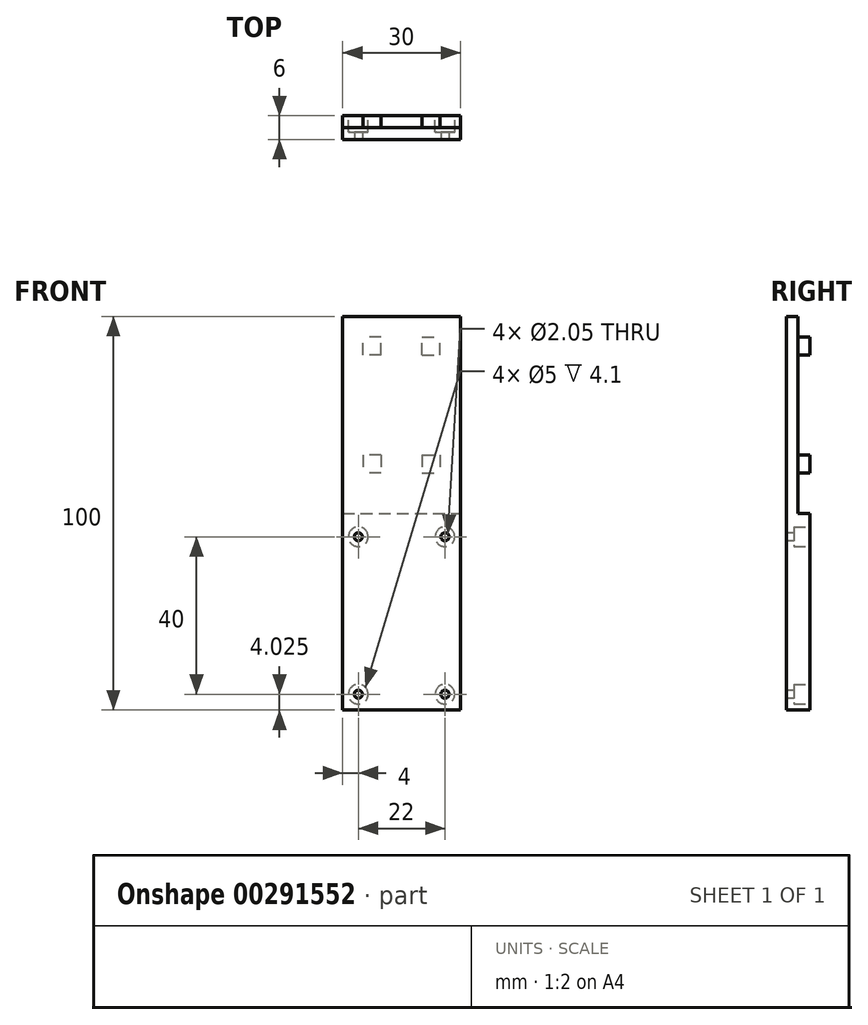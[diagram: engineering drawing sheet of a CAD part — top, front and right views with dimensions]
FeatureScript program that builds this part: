
annotation { "Feature Type Name" : "Feature", "Feature Type Description" : "" }
export const myFeature = defineFeature(function(context is Context, id is Id, definition is map)
    precondition{}
    {
        {
            var Q0;
            Q0=qCreatedBy(makeId("Top.planeOp"),FACE);
            var sketch = newSketch(context, id + "F0", { "sketchPlane" : qUnion([Q0])});
            skLineSegment(sketch, "E0.bottom", {"start": v(-15, 3) * mm, "end": v(15, 3) * mm});
            skLineSegment(sketch, "E0.top", {"start": v(-15, -3) * mm, "end": v(15, -3) * mm});
            skLineSegment(sketch, "E0.left", {"start": v(-15, 3) * mm, "end": v(-15, -3) * mm});
            skLineSegment(sketch, "E0.right", {"start": v(15, 3) * mm, "end": v(15, -3) * mm});
            skSolve(sketch);
        }
        {
            var Q0;
            Q0=qSketchRegion(id+"F0",true);
            extrude(context, id + "F1", {"entities" : qUnion([Q0]), "depth" : 100 * mm, "offsetDistance" : 25 * mm});
        }
        {
            var Q0;
            Q0=makeQuery(id+"F1.opExtrude","SWEPT_FACE",FACE,{"disambiguationData":[OSD([sQuery(id+"F0.wireOp",EDGE,"E0.top")])]});
            var sketch = newSketch(context, id + "F2", { "sketchPlane" : qUnion([Q0])});
            skCircle(sketch, "E1", {"center": v(11, 4.03) * mm, "radius": 1.02 * mm});
            skCircle(sketch, "E2", {"center": v(11, 44.03) * mm, "radius": 1.02 * mm});
            skCircle(sketch, "E3", {"center": v(-11, 44.03) * mm, "radius": 1.02 * mm});
            skCircle(sketch, "E4", {"center": v(-11, 4.03) * mm, "radius": 1.02 * mm});
            skSolve(sketch);
        }
        {
            var Q0;
            Q0=qSketchRegion(id+"F2",true);
            extrude(context, id + "F3", {"entities" : qUnion([Q0]), "operationType" : NewBodyOperationType.REMOVE, "endBound" : BoundingType.UP_TO_NEXT, "oppositeDirection" : true, "depth" : 25 * mm});
        }
        {
            var Q0;
            Q0=makeQuery(id+"F1.opExtrude","SWEPT_FACE",FACE,{"disambiguationData":[OSD([sQuery(id+"F0.wireOp",EDGE,"E0.right")])]});
            var sketch = newSketch(context, id + "F4", { "sketchPlane" : qUnion([Q0])});
            skLineSegment(sketch, "E5.bottom", {"start": v(0, 100) * mm, "end": v(3, 100) * mm});
            skLineSegment(sketch, "E5.top", {"start": v(0, 50) * mm, "end": v(3, 50) * mm});
            skLineSegment(sketch, "E5.left", {"start": v(0, 100) * mm, "end": v(0, 50) * mm});
            skLineSegment(sketch, "E5.right", {"start": v(3, 100) * mm, "end": v(3, 50) * mm});
            skSolve(sketch);
        }
        {
            var Q0;
            Q0 = qSketchRegion(id + "F4", true);
            extrude(context, id + "F5", {"entities" : qUnion([Q0]), "operationType" : NewBodyOperationType.REMOVE, "endBound" : BoundingType.UP_TO_NEXT, "oppositeDirection" : true, "depth" : 25 * mm, "offsetDistance" : 25 * mm});
        }
        {
            var Q0;
            Q0=makeQuery(id+"F5.boolean.opBoolean","COPY",FACE,{"derivedFrom":makeQuery(id+"F5.opExtrude","SWEPT_FACE",FACE,{"disambiguationData":[OSD([sQuery(id+"F4.wireOp",EDGE,"E5.left")])]})});
            var sketch = newSketch(context, id + "F6", { "sketchPlane" : qUnion([Q0])});
            skPoint(sketch, "E6.endSnap0", {"position": v(0, 100) * mm});
            skLineSegment(sketch, "E7.0", {"start": v(-5.2, 94.8) * mm, "end": v(-9.8, 94.8) * mm});
            skLineSegment(sketch, "E7.1", {"start": v(-5.2, 90.2) * mm, "end": v(-5.2, 94.8) * mm});
            skLineSegment(sketch, "E7.2", {"start": v(-5.2, 90.2) * mm, "end": v(-9.8, 90.2) * mm});
            skLineSegment(sketch, "E7.3", {"start": v(-9.8, 90.2) * mm, "end": v(-9.8, 94.8) * mm});
            skLineSegment(sketch, "E8.0", {"start": v(5.2, 94.8) * mm, "end": v(9.8, 94.8) * mm});
            skLineSegment(sketch, "E8.1", {"start": v(5.2, 90.2) * mm, "end": v(5.2, 94.8) * mm});
            skLineSegment(sketch, "E8.2", {"start": v(5.2, 90.2) * mm, "end": v(9.8, 90.2) * mm});
            skLineSegment(sketch, "E8.3", {"start": v(9.8, 90.2) * mm, "end": v(9.8, 94.8) * mm});
            skLineSegment(sketch, "E9.0", {"start": v(-9.8, 64.8) * mm, "end": v(-9.8, 60.2) * mm});
            skLineSegment(sketch, "E9.1", {"start": v(-5.2, 64.8) * mm, "end": v(-9.8, 64.8) * mm});
            skLineSegment(sketch, "E9.2", {"start": v(-5.2, 64.8) * mm, "end": v(-5.2, 60.2) * mm});
            skLineSegment(sketch, "E9.3", {"start": v(-5.2, 60.2) * mm, "end": v(-9.8, 60.2) * mm});
            skLineSegment(sketch, "E10.0", {"start": v(5.2, 64.8) * mm, "end": v(9.8, 64.8) * mm});
            skLineSegment(sketch, "E10.1", {"start": v(5.2, 64.8) * mm, "end": v(5.2, 60.2) * mm});
            skLineSegment(sketch, "E10.2", {"start": v(5.2, 60.2) * mm, "end": v(9.8, 60.2) * mm});
            skLineSegment(sketch, "E10.3", {"start": v(9.8, 64.8) * mm, "end": v(9.8, 60.2) * mm});
            skSolve(sketch);
        }
        {
            var Q0;
            Q0 = qSketchRegion(id + "F6", true);
            extrude(context, id + "F7", {"entities" : qUnion([Q0]), "operationType" : NewBodyOperationType.ADD, "depth" : 3 * mm, "offsetDistance" : 25 * mm});
        }
        {
            var Q0;
            Q0=makeQuery(id+"F1.opExtrude","SWEPT_FACE",FACE,{"disambiguationData":[OSD([sQuery(id+"F0.wireOp",EDGE,"E0.bottom")])]});
            var sketch = newSketch(context, id + "F8", { "sketchPlane" : qUnion([Q0])});
            skCircle(sketch, "E11", {"center": v(11, 44.03) * mm, "radius": 2.5 * mm});
            skCircle(sketch, "E12", {"center": v(-11, 44.03) * mm, "radius": 2.5 * mm});
            skCircle(sketch, "E13", {"center": v(-11, 4.03) * mm, "radius": 2.5 * mm});
            skCircle(sketch, "E14", {"center": v(11, 4.03) * mm, "radius": 2.5 * mm});
            skSolve(sketch);
        }
        {
            var Q0;
            Q0 = qSketchRegion(id + "F8", true);
            extrude(context, id + "F9", {"entities" : qUnion([Q0]), "operationType" : NewBodyOperationType.REMOVE, "oppositeDirection" : true, "depth" : 4.1 * mm, "offsetDistance" : 25 * mm});
        }
    });
